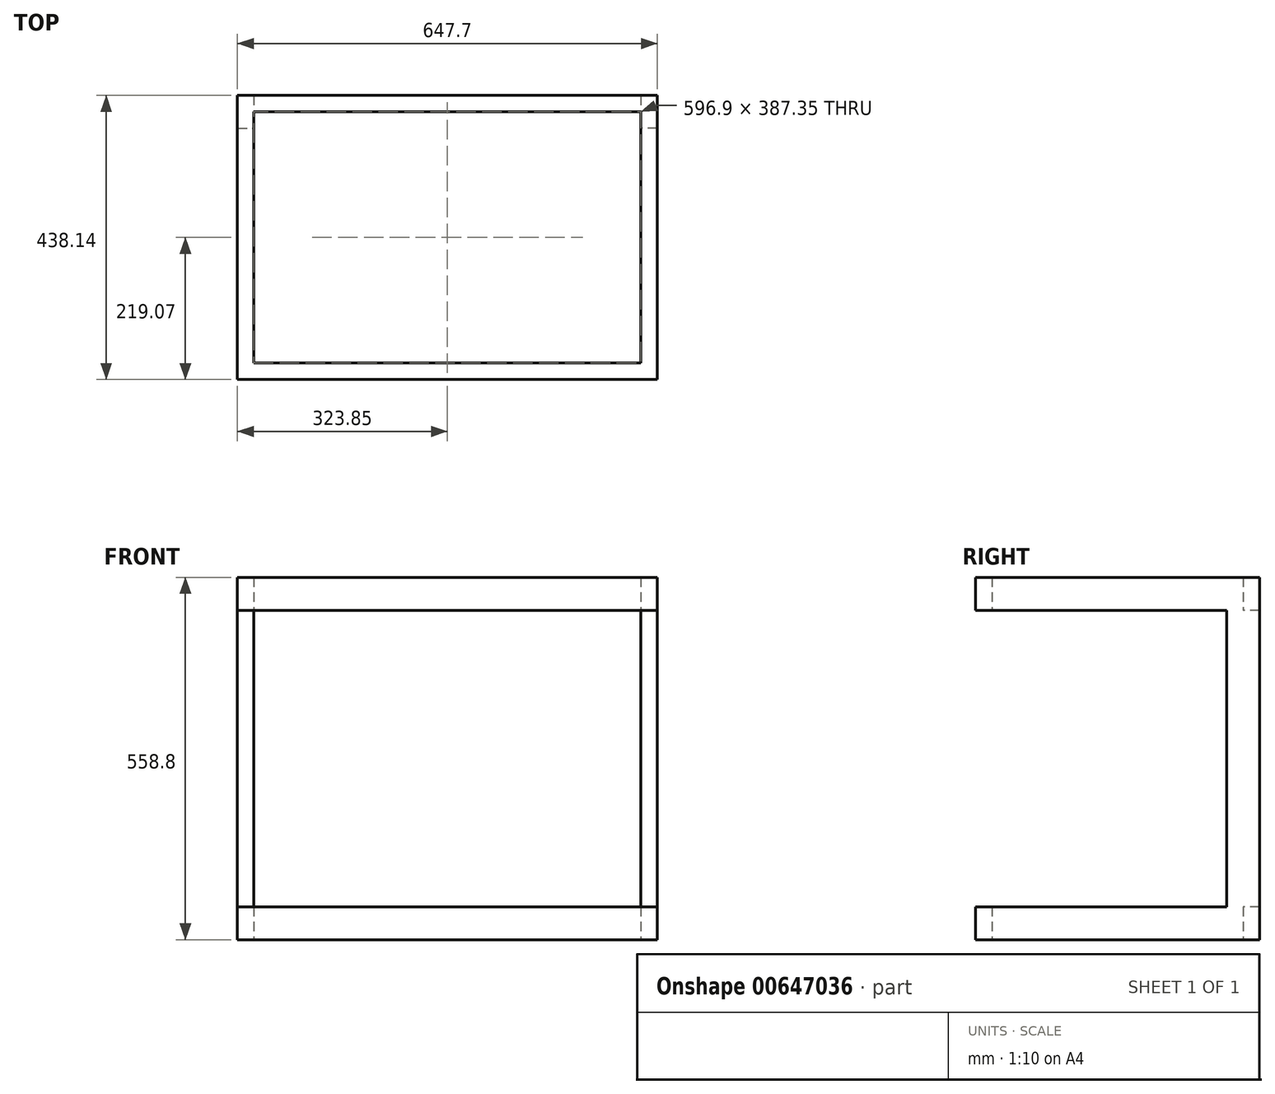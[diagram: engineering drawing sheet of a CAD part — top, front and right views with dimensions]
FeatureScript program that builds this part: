
annotation { "Feature Type Name" : "Feature", "Feature Type Description" : "" }
export const myFeature = defineFeature(function(context is Context, id is Id, definition is map)
    precondition{}
    {
        {
            var Q0;
            Q0=qCreatedBy(makeId("Top.planeOp"),FACE);
            var sketch = newSketch(context, id + "F0", { "sketchPlane" : qUnion([Q0])});
            skLineSegment(sketch, "E0.bottom", {"start": v(323.85, 219.07) * mm, "end": v(-323.85, 219.08) * mm});
            skLineSegment(sketch, "E0.top", {"start": v(323.85, -219.08) * mm, "end": v(-323.85, -219.07) * mm});
            skLineSegment(sketch, "E0.left", {"start": v(323.85, 219.07) * mm, "end": v(323.85, -219.08) * mm});
            skLineSegment(sketch, "E0.right", {"start": v(-323.85, 219.08) * mm, "end": v(-323.85, -219.07) * mm});
            skPoint(sketch, "E0.middle", {"position": v(0, 0) * mm});
            skLineSegment(sketch, "E1.bottom", {"start": v(298.45, 193.67) * mm, "end": v(-298.45, 193.68) * mm});
            skLineSegment(sketch, "E1.top", {"start": v(298.45, -193.67) * mm, "end": v(-298.45, -193.67) * mm});
            skLineSegment(sketch, "E1.left", {"start": v(298.45, 193.67) * mm, "end": v(298.45, -193.68) * mm});
            skLineSegment(sketch, "E1.right", {"start": v(-298.45, 193.68) * mm, "end": v(-298.45, -193.67) * mm});
            skSolve(sketch);
        }
        {
            var Q0;
            Q0=makeQuery(id+"F0.imprint","IMPRINT",FACE,{"disambiguationData":[TD([[makeQuery(id+"F0.imprint","IMPRINT",EDGE,{"derivedFrom":sQuery(id+"F0.wireOp",EDGE,"E0.bottom")}),1.0]])]});
            extrude(context, id + "F1", {"entities" : qUnion([Q0]), "depth" : 50.8 * mm, "offsetDistance" : 25.4 * mm});
        }
        {
            var Q0;
            Q0=makeQuery(id+"F1.opExtrude","CAP_FACE",FACE,{"disambiguationData":[OSD([sQuery(id+"F0.wireOp",EDGE,"E0.bottom"),sQuery(id+"F0.wireOp",EDGE,"E0.top"),sQuery(id+"F0.wireOp",EDGE,"E0.left"),sQuery(id+"F0.wireOp",EDGE,"E0.right"),sQuery(id+"F0.wireOp",EDGE,"E1.bottom"),sQuery(id+"F0.wireOp",EDGE,"E1.top"),sQuery(id+"F0.wireOp",EDGE,"E1.left"),sQuery(id+"F0.wireOp",EDGE,"E1.right")])],"isStart":false});
            var sketch = newSketch(context, id + "F2", { "sketchPlane" : qUnion([Q0])});
            skLineSegment(sketch, "E2.bottom", {"start": v(-323.85, 219.08) * mm, "end": v(-298.45, 219.08) * mm});
            skLineSegment(sketch, "E2.top", {"start": v(-323.85, 168.28) * mm, "end": v(-298.45, 168.28) * mm});
            skLineSegment(sketch, "E2.left", {"start": v(-323.85, 219.08) * mm, "end": v(-323.85, 168.28) * mm});
            skLineSegment(sketch, "E2.right", {"start": v(-298.45, 219.08) * mm, "end": v(-298.45, 168.28) * mm});
            skLineSegment(sketch, "E3.bottom", {"start": v(323.85, 219.07) * mm, "end": v(298.45, 219.07) * mm});
            skLineSegment(sketch, "E3.top", {"start": v(323.85, 168.27) * mm, "end": v(298.45, 168.27) * mm});
            skLineSegment(sketch, "E3.left", {"start": v(323.85, 219.07) * mm, "end": v(323.85, 168.27) * mm});
            skLineSegment(sketch, "E3.right", {"start": v(298.45, 219.07) * mm, "end": v(298.45, 168.27) * mm});
            skSolve(sketch);
        }
        {
            var Q0;
            {var subQ3=sQuery(id+"F2.wireOp",EDGE,"E2.bottom");Q0=makeQuery(id+"F2.imprint","IMPRINT",FACE,{"disambiguationData":[TD([[makeQuery(id+"F2.imprint","IMPRINT",EDGE,{"derivedFrom":subQ3}),1.0]])]});}
            var Q1;
            {var subQ3=sQuery(id+"F2.wireOp",EDGE,"E3.bottom");Q1=makeQuery(id+"F2.imprint","IMPRINT",FACE,{"disambiguationData":[TD([[makeQuery(id+"F2.imprint","IMPRINT",EDGE,{"derivedFrom":subQ3}),1.0]])]});}
            extrude(context, id + "F3", {"entities" : qUnion([Q0, Q1]), "operationType" : NewBodyOperationType.ADD, "depth" : 508 * mm, "offsetDistance" : 25.4 * mm});
        }
        {
            var Q0;
            Q0=makeQuery(id+"F3.opExtrude","SWEPT_FACE",FACE,{"disambiguationData":[OSD([sQuery(id+"F2.wireOp",EDGE,"E2.top")])]});
            var sketch = newSketch(context, id + "F4", { "sketchPlane" : qUnion([Q0])});
            skLineSegment(sketch, "E4.bottom", {"start": v(-323.85, 558.8) * mm, "end": v(-298.45, 558.8) * mm});
            skLineSegment(sketch, "E4.top", {"start": v(-323.85, 508) * mm, "end": v(-298.45, 508) * mm});
            skLineSegment(sketch, "E4.left", {"start": v(-323.85, 558.8) * mm, "end": v(-323.85, 508) * mm});
            skLineSegment(sketch, "E4.right", {"start": v(-298.45, 558.8) * mm, "end": v(-298.45, 508) * mm});
            skSolve(sketch);
        }
        {
            var Q0;
            Q0 = qSketchRegion(id + "F4", true);
            extrude(context, id + "F5", {"entities" : qUnion([Q0]), "operationType" : NewBodyOperationType.ADD, "depth" : 374.65 * mm, "offsetDistance" : 25.4 * mm});
        }
        {
            var Q0;
            Q0=makeQuery(id+"F3.opExtrude","SWEPT_FACE",FACE,{"disambiguationData":[OSD([sQuery(id+"F2.wireOp",EDGE,"E3.top")])]});
            var sketch = newSketch(context, id + "F6", { "sketchPlane" : qUnion([Q0])});
            skLineSegment(sketch, "E5.bottom", {"start": v(298.45, 558.8) * mm, "end": v(323.85, 558.8) * mm});
            skLineSegment(sketch, "E5.top", {"start": v(298.45, 508) * mm, "end": v(323.85, 508) * mm});
            skLineSegment(sketch, "E5.left", {"start": v(298.45, 558.8) * mm, "end": v(298.45, 508) * mm});
            skLineSegment(sketch, "E5.right", {"start": v(323.85, 558.8) * mm, "end": v(323.85, 508) * mm});
            skSolve(sketch);
        }
        {
            var Q0;
            Q0 = qSketchRegion(id + "F6", true);
            extrude(context, id + "F7", {"entities" : qUnion([Q0]), "operationType" : NewBodyOperationType.ADD, "depth" : 387.35 * mm, "offsetDistance" : 25.4 * mm});
        }
        {
            var Q0;
            Q0=makeQuery(id+"F7.boolean.opBoolean","MERGE",FACE,{"derivedFrom":[makeQuery(id+"F3.boolean.opBoolean","MERGE",FACE,{"derivedFrom":[makeQuery(id+"F1.opExtrude","SWEPT_FACE",FACE,{"disambiguationData":[OSD([sQuery(id+"F0.wireOp",EDGE,"E1.left")])]}),makeQuery(id+"F3.opExtrude","SWEPT_FACE",FACE,{"disambiguationData":[OSD([sQuery(id+"F2.wireOp",EDGE,"E3.right")])]})]}),makeQuery(id+"F7.opExtrude","SWEPT_FACE",FACE,{"disambiguationData":[OSD([sQuery(id+"F6.wireOp",EDGE,"E5.left")])]})]});
            var sketch = newSketch(context, id + "F8", { "sketchPlane" : qUnion([Q0])});
            skLineSegment(sketch, "E6.bottom", {"start": v(219.08, 558.8) * mm, "end": v(193.68, 558.8) * mm});
            skLineSegment(sketch, "E6.top", {"start": v(219.08, 508) * mm, "end": v(193.68, 508) * mm});
            skLineSegment(sketch, "E6.left", {"start": v(219.08, 558.8) * mm, "end": v(219.08, 508) * mm});
            skLineSegment(sketch, "E6.right", {"start": v(193.68, 558.8) * mm, "end": v(193.68, 508) * mm});
            skSolve(sketch);
        }
        {
            var Q0;
            Q0 = qSketchRegion(id + "F8", true);
            extrude(context, id + "F9", {"entities" : qUnion([Q0]), "operationType" : NewBodyOperationType.ADD, "depth" : 622.3 * mm, "offsetDistance" : 25.4 * mm});
        }
        {
            var Q0;
            Q0=makeQuery(id+"F7.boolean.opBoolean","MERGE",FACE,{"derivedFrom":[makeQuery(id+"F3.boolean.opBoolean","MERGE",FACE,{"derivedFrom":[makeQuery(id+"F1.opExtrude","SWEPT_FACE",FACE,{"disambiguationData":[OSD([sQuery(id+"F0.wireOp",EDGE,"E1.left")])]}),makeQuery(id+"F3.opExtrude","SWEPT_FACE",FACE,{"disambiguationData":[OSD([sQuery(id+"F2.wireOp",EDGE,"E3.right")])]})]}),makeQuery(id+"F7.opExtrude","SWEPT_FACE",FACE,{"disambiguationData":[OSD([sQuery(id+"F6.wireOp",EDGE,"E5.left")])]})]});
            var sketch = newSketch(context, id + "F10", { "sketchPlane" : qUnion([Q0])});
            skLineSegment(sketch, "E7.bottom", {"start": v(-219.07, 558.8) * mm, "end": v(-193.67, 558.8) * mm});
            skLineSegment(sketch, "E7.top", {"start": v(-219.07, 508) * mm, "end": v(-193.67, 508) * mm});
            skLineSegment(sketch, "E7.left", {"start": v(-219.07, 558.8) * mm, "end": v(-219.07, 508) * mm});
            skLineSegment(sketch, "E7.right", {"start": v(-193.67, 558.8) * mm, "end": v(-193.67, 508) * mm});
            skSolve(sketch);
        }
        {
            var Q0;
            Q0 = qSketchRegion(id + "F10", true);
            extrude(context, id + "F11", {"entities" : qUnion([Q0]), "operationType" : NewBodyOperationType.ADD, "depth" : 622.3 * mm, "offsetDistance" : 25.4 * mm});
        }
    });
